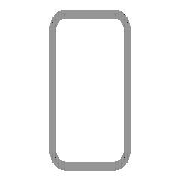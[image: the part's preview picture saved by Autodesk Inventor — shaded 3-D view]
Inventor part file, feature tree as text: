
AUTODESK INVENTOR PART (.ipt)
format: ipt  version: 2025 (Build 290162010, 162A)  size: 133,120 bytes
history: native  units: mm (DEFAULTED — no unit token found)
features: other x4, sketch x1, plane x1
ambient origin geometry x8: Origin, YZ Plane, XZ Plane, XY Plane, X Axis, Y Axis, Z Axis, Center Point
bodies: Solid1 (feature_tree), Body (feature_tree)
feature tree (6):
  parser-record x1  (decoder bookkeeping rows leaked as tree rows — omitted from the tree; the rows remain in map.json)
  other  "Driven Length"
  other  "Start Plane"
  other  "End Plane"
  sketch  "Sketch3"  dims[d3=2876.273mm d4=0.0mm d7=6.0mm d9=20.0mm d11=40.0mm d12=3.0mm d13=-0.0mm d14=2876.273mm d15=10.0mm d16=20.0mm d17=90.0deg d18=2876.273mm]
  plane  "Work Plane3"
